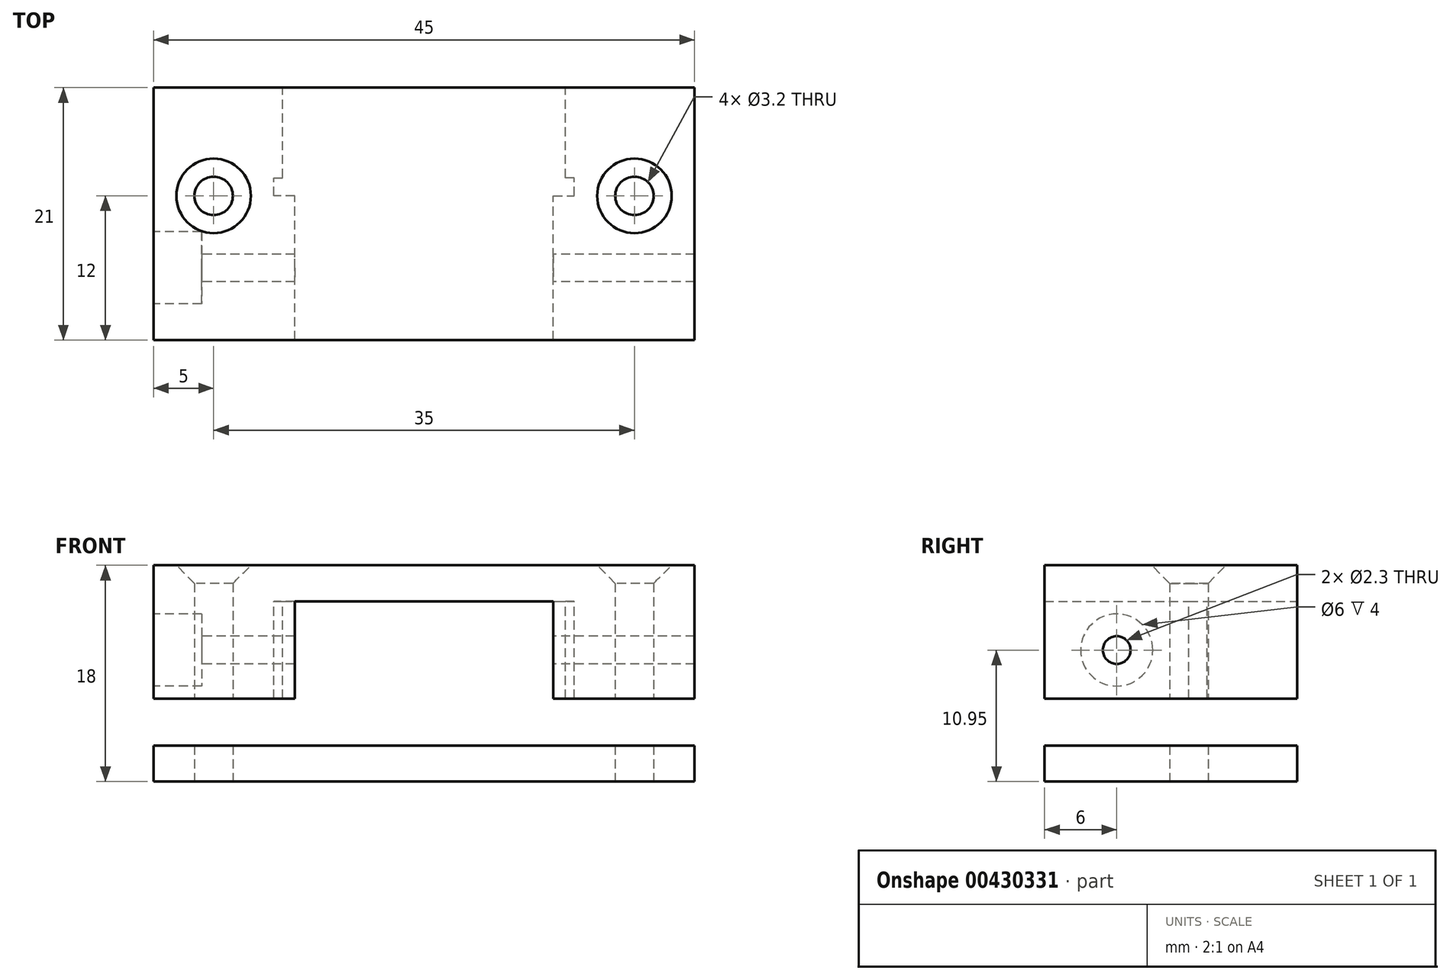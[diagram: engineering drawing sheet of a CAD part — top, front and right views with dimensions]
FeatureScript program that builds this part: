
annotation { "Feature Type Name" : "Feature", "Feature Type Description" : "" }
export const myFeature = defineFeature(function(context is Context, id is Id, definition is map)
    precondition{}
    {
        {
            var Q0;
            Q0=qCreatedBy(makeId("Top.planeOp"),FACE);
            var sketch = newSketch(context, id + "F0", { "sketchPlane" : qUnion([Q0])});
            skLineSegment(sketch, "E0", {"start": v(10.75, -12) * mm, "end": v(10.75, 0) * mm});
            skLineSegment(sketch, "E1", {"start": v(10.75, 0) * mm, "end": v(12.5, 0) * mm});
            skLineSegment(sketch, "E2", {"start": v(12.5, 0) * mm, "end": v(12.5, 1.5) * mm});
            skLineSegment(sketch, "E3", {"start": v(12.5, 1.5) * mm, "end": v(11.75, 1.5) * mm});
            skLineSegment(sketch, "E4", {"start": v(11.75, 1.5) * mm, "end": v(11.75, 9) * mm});
            skLineSegment(sketch, "E5.MirrorCS", {"start": v(-12.5, 0) * mm, "end": v(-12.5, 1.5) * mm});
            skLineSegment(sketch, "E6.MirrorCS", {"start": v(-10.75, 0) * mm, "end": v(-12.5, 0) * mm});
            skLineSegment(sketch, "E7.MirrorCS", {"start": v(-12.5, 1.5) * mm, "end": v(-11.75, 1.5) * mm});
            skLineSegment(sketch, "E8.MirrorCS", {"start": v(-10.75, -12) * mm, "end": v(-10.75, 0) * mm});
            skLineSegment(sketch, "E9.MirrorCS", {"start": v(-11.75, 1.5) * mm, "end": v(-11.75, 9) * mm});
            skLineSegment(sketch, "E10.bottom", {"start": v(-22.5, 9) * mm, "end": v(22.5, 9) * mm});
            skLineSegment(sketch, "E10.top", {"start": v(-22.5, -12) * mm, "end": v(22.5, -12) * mm});
            skLineSegment(sketch, "E10.left", {"start": v(-22.5, 9) * mm, "end": v(-22.5, -12) * mm});
            skLineSegment(sketch, "E10.right", {"start": v(22.5, 9) * mm, "end": v(22.5, -12) * mm});
            skCircle(sketch, "E11", {"center": v(17.5, 0) * mm, "radius": 1.6 * mm});
            skCircle(sketch, "E12.MirrorC", {"center": v(-17.5, 0) * mm, "radius": 1.6 * mm});
            skSolve(sketch);
        }
        {
            var Q0;
            Q0 = qSketchRegion(id + "F0", true);
            extrude(context, id + "F1", {"entities" : qUnion([Q0]), "depth" : 3 * mm, "offsetDistance" : 25 * mm});
        }
        {
            var Q0;
            Q0=makeQuery(id+"F1.opExtrude","SWEPT_BODY",BODY,{"disambiguationData":[OSD([sQuery(id+"F0.wireOp",EDGE,"E10.bottom"),sQuery(id+"F0.wireOp",EDGE,"E10.top"),sQuery(id+"F0.wireOp",EDGE,"E10.left"),sQuery(id+"F0.wireOp",EDGE,"E10.right"),sQuery(id+"F0.wireOp",EDGE,"E11"),sQuery(id+"F0.wireOp",EDGE,"E12.MirrorC")])]});
            transform(context, id + "F2", {"entities" : qUnion([Q0]), "transformType" : TransformType.TRANSLATION_3D, "dx" : 0 * mm, "dy" : 0 * mm, "dz" : -15 * mm, "makeCopy" : true});
        }
        {
            var Q0;
            Q0=makeQuery(id+"F0.imprint","IMPRINT",FACE,{"disambiguationData":[TD([[makeQuery(id+"F0.imprint","IMPRINT",EDGE,{"derivedFrom":sQuery(id+"F0.wireOp",EDGE,"E5.MirrorCS")}),1.0]])]});
            var Q1;
            {var subQ3=sQuery(id+"F0.wireOp",EDGE,"E0");Q1=makeQuery(id+"F0.imprint","IMPRINT",FACE,{"disambiguationData":[TD([[makeQuery(id+"F0.imprint","IMPRINT",EDGE,{"derivedFrom":subQ3}),-1.0]])]});}
            extrude(context, id + "F3", {"entities" : qUnion([Q0, Q1]), "operationType" : NewBodyOperationType.ADD, "oppositeDirection" : true, "depth" : 8.1 * mm, "offsetDistance" : 25 * mm});
        }
        {
            var Q0;
            Q0=makeQuery(id+"F1.opExtrude","CAP_EDGE",EDGE,{"disambiguationData":[OSD([sQuery(id+"F0.wireOp",EDGE,"E12.MirrorC")])],"isStart":false});
            var Q1;
            Q1=makeQuery(id+"F1.opExtrude","CAP_EDGE",EDGE,{"disambiguationData":[OSD([sQuery(id+"F0.wireOp",EDGE,"E11")])],"isStart":false});
            chamfer(context, id + "F4", {"entities" : qUnion([Q0, Q1]), "width" : 1.5 * mm, "tangentPropagation" : true});
        }
        {
            var Q0;
            {var subQ0=sQuery(id+"F0.wireOp",EDGE,"E10.left");Q0=makeQuery(id+"F3.boolean.opBoolean","MERGE",FACE,{"derivedFrom":[makeQuery(id+"F1.opExtrude","SWEPT_FACE",FACE,{"disambiguationData":[OSD([subQ0])]}),makeQuery(id+"F3.opExtrude","SWEPT_FACE",FACE,{"disambiguationData":[OSD([subQ0])]})]});}
            var sketch = newSketch(context, id + "F5", { "sketchPlane" : qUnion([Q0])});
            skCircle(sketch, "E13", {"center": v(6, -4.05) * mm, "radius": 1.15 * mm});
            skLineSegment(sketch, "E14", {"start": v(0, -4.05) * mm, "end": v(12, -4.05) * mm, "construction": true});
            skCircle(sketch, "E15", {"center": v(6, -4.05) * mm, "radius": 3 * mm});
            skSolve(sketch);
        }
        {
            var Q0;
            Q0=makeQuery(id+"F5.imprint","IMPRINT",FACE,{"disambiguationData":[TD([[makeQuery(id+"F5.imprint","IMPRINT",EDGE,{"derivedFrom":sQuery(id+"F5.wireOp",EDGE,"E13")}),1.0]])]});
            extrude(context, id + "F6", {"entities" : qUnion([Q0]), "operationType" : NewBodyOperationType.REMOVE, "endBound" : BoundingType.THROUGH_ALL, "oppositeDirection" : true, "depth" : 25 * mm, "offsetDistance" : 25 * mm});
        }
        {
            var Q0;
            Q0=makeQuery(id+"F5.imprint","IMPRINT",FACE,{"disambiguationData":[TD([[makeQuery(id+"F5.imprint","IMPRINT",EDGE,{"derivedFrom":sQuery(id+"F5.wireOp",EDGE,"E13")}),-1.0]])]});
            extrude(context, id + "F7", {"entities" : qUnion([Q0]), "operationType" : NewBodyOperationType.REMOVE, "oppositeDirection" : true, "depth" : 4 * mm, "offsetDistance" : 25 * mm});
        }
    });
